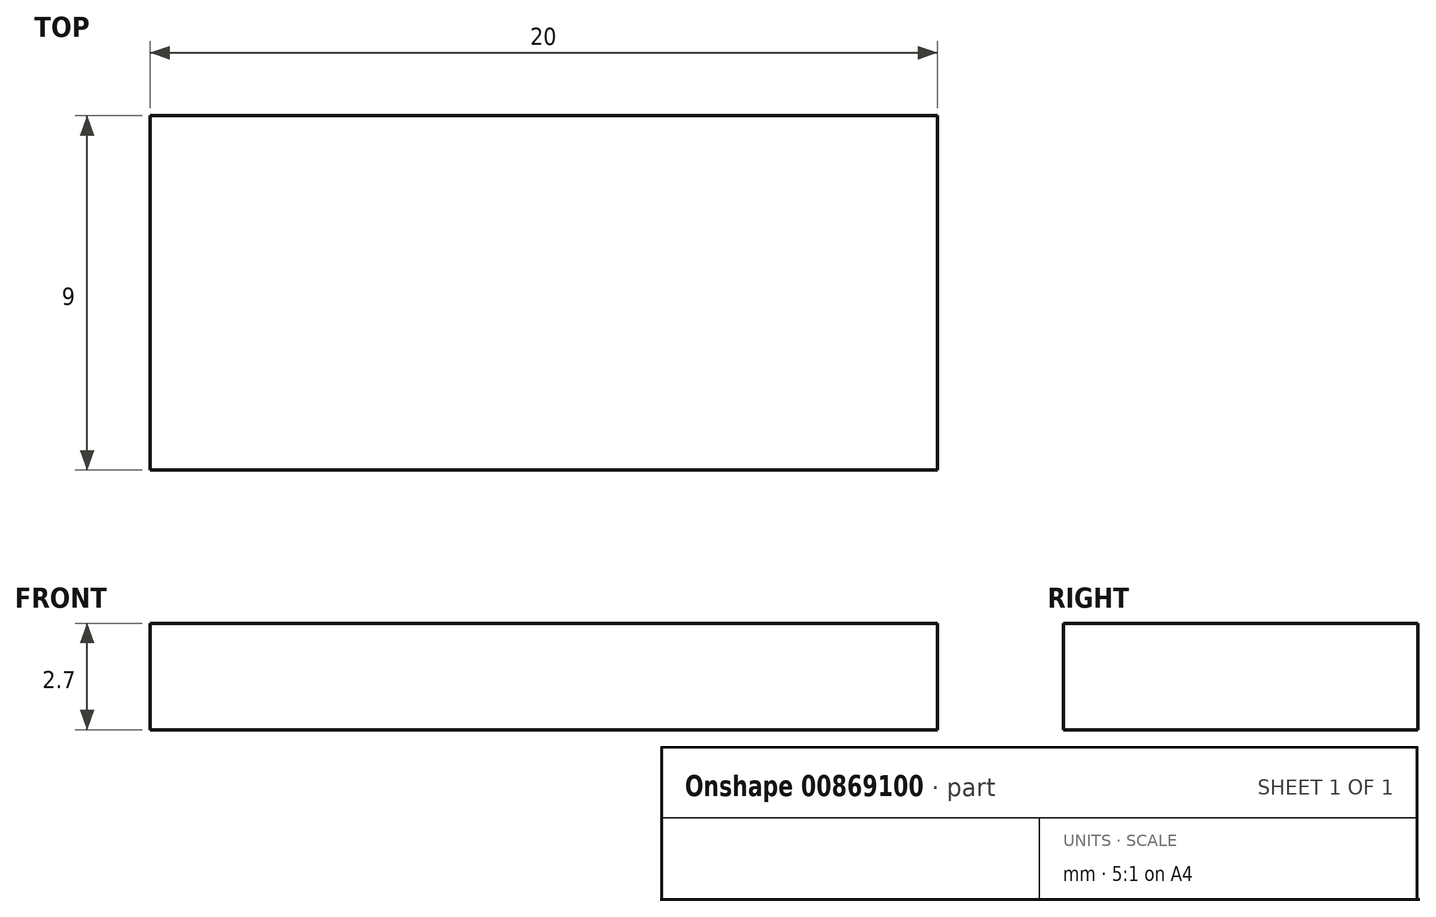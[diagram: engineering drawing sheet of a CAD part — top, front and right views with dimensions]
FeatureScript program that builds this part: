
annotation { "Feature Type Name" : "Feature", "Feature Type Description" : "" }
export const myFeature = defineFeature(function(context is Context, id is Id, definition is map)
    precondition{}
    {
        {
            var Q0;
            Q0=qCreatedBy(makeId("Top.planeOp"),FACE);
            var sketch = newSketch(context, id + "F0", { "sketchPlane" : qUnion([Q0])});
            skLineSegment(sketch, "E0.bottom", {"start": v(-3.76, 5.01) * mm, "end": v(16.24, 5.01) * mm});
            skLineSegment(sketch, "E0.top", {"start": v(-3.76, -3.99) * mm, "end": v(16.24, -3.99) * mm});
            skLineSegment(sketch, "E0.left", {"start": v(-3.76, 5.01) * mm, "end": v(-3.76, -3.99) * mm});
            skLineSegment(sketch, "E0.right", {"start": v(16.24, 5.01) * mm, "end": v(16.24, -3.99) * mm});
            skSolve(sketch);
        }
        {
            var Q0;
            Q0 = qSketchRegion(id + "F0", true);
            extrude(context, id + "F1", {"entities" : qUnion([Q0]), "depth" : 2.7 * mm, "offsetDistance" : 25 * mm});
        }
    });
